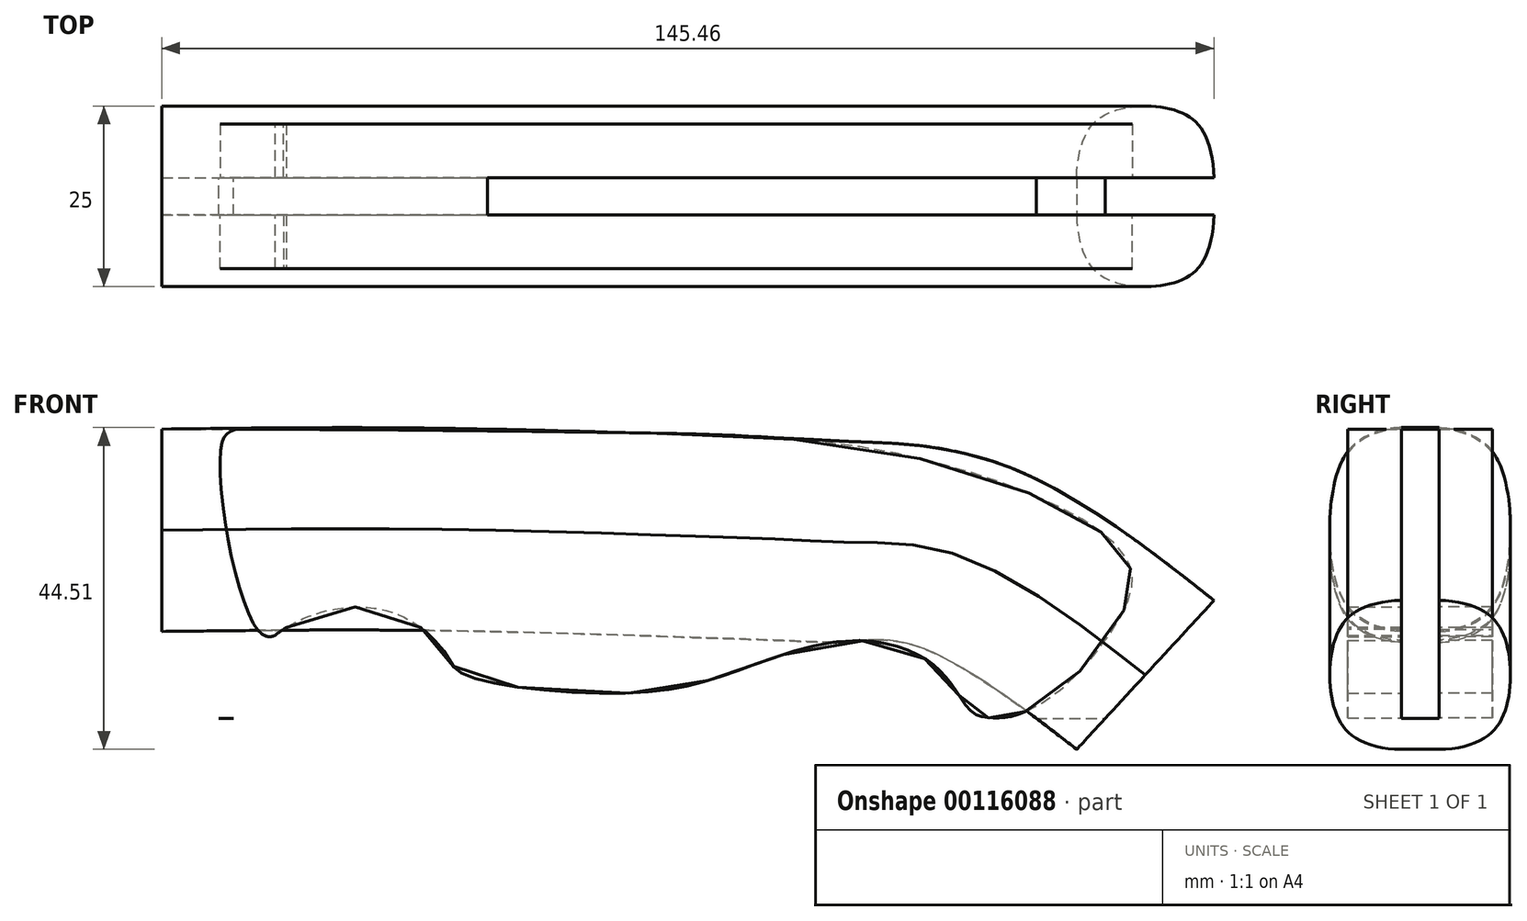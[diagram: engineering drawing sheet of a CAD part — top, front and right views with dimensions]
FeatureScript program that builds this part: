
annotation { "Feature Type Name" : "Feature", "Feature Type Description" : "" }
export const myFeature = defineFeature(function(context is Context, id is Id, definition is map)
    precondition{}
    {
        {
            var Q0;
            Q0=qCreatedBy(makeId("Front.planeOp"),FACE);
            var sketch = newSketch(context, id + "F0", { "sketchPlane" : qUnion([Q0])});
            skLineSegment(sketch, "E0", {"start": v(0, 40) * mm, "end": v(-250, 40) * mm});
            skLineSegment(sketch, "E1", {"start": v(-250, 40) * mm, "end": v(-250, 0) * mm});
            skLineSegment(sketch, "E2", {"start": v(-250, 0) * mm, "end": v(0, 0) * mm});
            skLineSegment(sketch, "E3", {"start": v(0, 0) * mm, "end": v(0, 40) * mm});
            skSolve(sketch);
        }
        {
            var Q0;
            Q0=qCreatedBy(makeId("Front.planeOp"),FACE);
            var sketch = newSketch(context, id + "F1", { "sketchPlane" : qUnion([Q0])});
            skLineSegment(sketch, "E4", {"start": v(-140.13, 40) * mm, "end": v(-10.13, 40) * mm, "construction": true});
            skLineSegment(sketch, "E5", {"start": v(-10.13, 40) * mm, "end": v(-10.13, 0) * mm, "construction": true});
            skFitSpline(sketch, "E6", {"points": [v(-195.15, 40) * mm, v(-214.61, 38.5) * mm, v(-226.5, 36.65) * mm, v(-250, 29) * mm], "startDerivative": vector(-36.4, 0) * mm, "endDerivative": vector(-83.44, -41.3) * mm});
            skLineSegment(sketch, "E7", {"start": v(-250, 40) * mm, "end": v(-250, 29) * mm, "construction": true});
            skFitSpline(sketch, "E8", {"points": [v(-250, 29) * mm, v(-237.9, 14.88) * mm, v(-219.9, 6.53) * mm, v(-197.47, 2.44) * mm, v(-140.13, -0.02) * mm], "startDerivative": vector(33.25, -72.74) * mm, "endDerivative": vector(161.21, 0) * mm});
            skFitSpline(sketch, "E9", {"points": [v(-140.13, -0.02) * mm, v(-137.85, 7.38) * mm, v(-129.23, 14.28) * mm, v(-117.32, 14.35) * mm, v(-110.68, 8.8) * mm, v(-108.34, 6.11) * mm, v(-85.42, 3.47) * mm, v(-71.01, 6.36) * mm, v(-55.73, 10.69) * mm, v(-45.11, 8.6) * mm, v(-40.68, 4.49) * mm, v(-37.73, 0.68) * mm, v(-32.41, 0.28) * mm, v(-22.8, 4.17) * mm, v(-12.46, 13.56) * mm, v(-11.48, 17.06) * mm, v(-13.01, 19.89) * mm, v(-23.92, 28.18) * mm, v(-50.74, 37.07) * mm, v(-90.96, 39.53) * mm, v(-140.13, 40) * mm], "startDerivative": vector(3.13, 131.36) * mm, "endDerivative": vector(-602.52, 0) * mm});
            skLineSegment(sketch, "E10", {"start": v(-195.15, 40) * mm, "end": v(-140.13, 40) * mm});
            skLineSegment(sketch, "E11", {"start": v(-140.13, 40) * mm, "end": v(-142.13, 40) * mm});
            skLineSegment(sketch, "E12", {"start": v(-142.13, 40) * mm, "end": v(-142.13, -0.02) * mm});
            skSolve(sketch);
        }
        {
            var Q0;
            Q0=qCreatedBy(makeId("Front.planeOp"),FACE);
            var sketch = newSketch(context, id + "F2", { "sketchPlane" : qUnion([Q0])});
            skFitSpline(sketch, "E13", {"points": [v(-139.83, 0) * mm, v(-137.7, 7.55) * mm, v(-129.23, 14.28) * mm, v(-117.32, 14.35) * mm, v(-110.68, 8.8) * mm, v(-108.34, 6.11) * mm, v(-85.42, 3.47) * mm, v(-71.01, 6.36) * mm, v(-55.73, 10.69) * mm, v(-45.11, 8.6) * mm, v(-40.68, 4.49) * mm, v(-37.73, 0.68) * mm, v(-35.14, 0.02) * mm, v(-32.41, 0.28) * mm, v(-25.38, 4.26) * mm, v(-16.97, 14.98) * mm, v(-15.84, 19.55) * mm, v(-17.11, 22.79) * mm, v(-23.92, 28.18) * mm, v(-50.74, 37.07) * mm, v(-90.96, 39.53) * mm, v(-139.08, 40) * mm], "startDerivative": vector(3.14, 131.36) * mm, "endDerivative": vector(-602.52, 0) * mm});
            skFitSpline(sketch, "E14", {"points": [v(-139.08, 40) * mm, v(-140.85, 39.45) * mm, v(-141.8, 37.79) * mm, v(-140.36, 22.3) * mm, v(-136.2, 11.67) * mm, v(-134.7, 11.32) * mm, v(-133.98, 11.7) * mm, v(-132.8, 12.56) * mm], "startDerivative": vector(-24.87, 0.07) * mm, "endDerivative": vector(13.86, 8) * mm});
            skSolve(sketch);
        }
        {
            var Q0;
            Q0=qCreatedBy(makeId("Front.planeOp"),FACE);
            var sketch = newSketch(context, id + "F3", { "sketchPlane" : qUnion([Q0])});
            skFitSpline(sketch, "E15", {"points": [v(-141.52, 25.66) * mm, v(-111.48, 25.66) * mm, v(-71.98, 24.55) * mm, v(-50, 23.16) * mm, v(-32.48, 18.15) * mm, v(-8.01, 0) * mm], "startDerivative": vector(127.42, 1.18) * mm, "endDerivative": vector(72.27, -65.29) * mm});
            skSolve(sketch);
        }
        {
            var Q0;
            Q0=qCreatedBy(makeId("Right.planeOp"),FACE);
            cPlane(context, id + "F4", {"entities" : qUnion([Q0]), "cplaneType" : CPlaneType.OFFSET, "offset" : 150 * mm, "oppositeDirection" : true, "width" : 150 * mm, "height" : 150 * mm});
        }
        {
            var Q0;
            Q0=qCreatedBy(id+"F4.planeOp",FACE);
            var sketch = newSketch(context, id + "F5", { "sketchPlane" : qUnion([Q0])});
            skLineSegment(sketch, "E16", {"start": v(0, 40) * mm, "end": v(0, 26) * mm, "construction": true});
            skLineSegment(sketch, "E17", {"start": v(0, 26) * mm, "end": v(12.5, 26) * mm, "construction": true});
            skFitSpline(sketch, "E18", {"points": [v(2.6, 40) * mm, v(8.74, 38) * mm, v(11.41, 33.88) * mm, v(12.5, 26) * mm], "startDerivative": vector(21.5, 0.1) * mm, "endDerivative": vector(-0.14, -22.75) * mm});
            skFitSpline(sketch, "E19.MirrorCS", {"points": [v(2.6, 12) * mm, v(8.74, 14) * mm, v(11.41, 18.12) * mm, v(12.5, 26) * mm], "startDerivative": vector(21.5, -0.1) * mm, "endDerivative": vector(-0.14, 22.75) * mm});
            skLineSegment(sketch, "E20.MirrorCS", {"start": v(0, 12) * mm, "end": v(0, 26) * mm, "construction": true});
            skFitSpline(sketch, "E21.MirrorCS", {"points": [v(2.6, 40) * mm, v(8.74, 38) * mm, v(11.41, 33.88) * mm, v(12.5, 26) * mm], "startDerivative": vector(21.5, 0.1) * mm, "endDerivative": vector(-0.14, -22.75) * mm});
            skFitSpline(sketch, "E22.MirrorCS", {"points": [v(-2.6, 40) * mm, v(-8.74, 38) * mm, v(-11.41, 33.88) * mm, v(-12.5, 26) * mm], "startDerivative": vector(-21.5, 0.1) * mm, "endDerivative": vector(0.14, -22.75) * mm});
            skFitSpline(sketch, "E23.MirrorCS", {"points": [v(-2.6, 12) * mm, v(-8.74, 14) * mm, v(-11.41, 18.12) * mm, v(-12.5, 26) * mm], "startDerivative": vector(-21.5, -0.1) * mm, "endDerivative": vector(0.14, 22.75) * mm});
            skLineSegment(sketch, "E24", {"start": v(2.6, 12) * mm, "end": v(-2.6, 12) * mm});
            skLineSegment(sketch, "E25", {"start": v(2.6, 40) * mm, "end": v(-2.6, 40) * mm});
            skSolve(sketch);
        }
        {
            var Q0;
            Q0=makeQuery(id+"F5.imprint","IMPRINT",FACE,{"disambiguationData":[TD([[makeQuery(id+"F5.imprint","IMPRINT",EDGE,{"derivedFrom":sQuery(id+"F5.wireOp",EDGE,"E19.MirrorCS")}),1.0]])]});
            var Q1;
            Q1=sQuery(id+"F3.wireOp",EDGE,"E15");
            sweep(context, id + "F6", {"profiles" : qUnion([Q0]), "path" : qUnion([Q1])});
        }
        {
            var Q0;
            Q0=makeQuery(id+"F1.imprint","IMPRINT",FACE,{"disambiguationData":[TD([[makeQuery(id+"F1.imprint","IMPRINT",EDGE,{"derivedFrom":sQuery(id+"F1.wireOp",EDGE,"E6")}),1.0]])]});
            extrude(context, id + "F7", {"entities" : qUnion([Q0]), "endBound" : BoundingType.SYMMETRIC, "depth" : 5.2 * mm});
        }
        {
            var Q0;
            Q0=makeQuery(id+"F7.opExtrude","CAP_EDGE",EDGE,{"disambiguationData":[OSD([sQuery(id+"F1.wireOp",EDGE,"E8")])],"isStart":false});
            var Q1;
            Q1=makeQuery(id+"F7.opExtrude","CAP_EDGE",EDGE,{"disambiguationData":[OSD([sQuery(id+"F1.wireOp",EDGE,"E8")])],"isStart":true});
            chamfer(context, id + "F8", {"entities" : qUnion([Q0, Q1]), "chamferType" : ChamferType.TWO_OFFSETS, "width1" : 20 * mm, "oppositeDirection" : false, "width2" : 2.6 * mm, "tangentPropagation" : true});
        }
        {
            var Q0;
            {var subQ0=sQuery(id+"F1.wireOp",EDGE,"E9");Q0=makeQuery(id+"F1.imprint","IMPRINT",FACE,{"disambiguationData":[TD([[makeQuery(id+"F1.imprint","IMPRINT",EDGE,{"derivedFrom":subQ0}),1.0]])]});}
            extrude(context, id + "F9", {"entities" : qUnion([Q0]), "operationType" : NewBodyOperationType.ADD, "endBound" : BoundingType.SYMMETRIC, "depth" : 5.2 * mm});
        }
        {
            var Q0;
            Q0=makeQuery(id+"F2.imprint","IMPRINT",FACE,{"disambiguationData":[TD([[makeQuery(id+"F2.imprint","IMPRINT",EDGE,{"derivedFrom":sQuery(id+"F2.wireOp",EDGE,"E13")}),1.0]])]});
            extrude(context, id + "F10", {"entities" : qUnion([Q0]), "endBound" : BoundingType.SYMMETRIC, "depth" : 20 * mm});
        }
        {
            var Q0;
            Q0 = qSketchRegion(id + "F0", true);
            extrude(context, id + "F11", {"entities" : qUnion([Q0]), "operationType" : NewBodyOperationType.REMOVE, "endBound" : BoundingType.SYMMETRIC, "depth" : 5.2 * mm});
        }
    });
